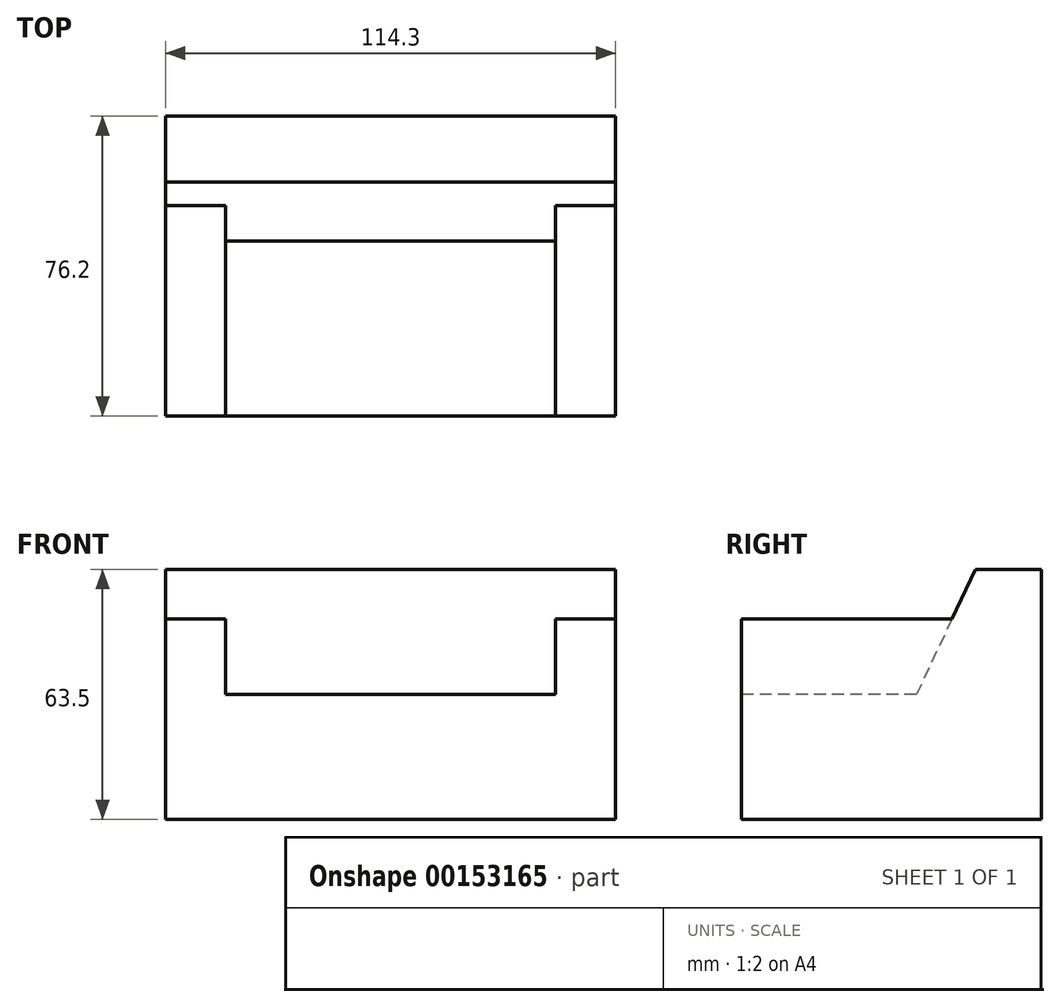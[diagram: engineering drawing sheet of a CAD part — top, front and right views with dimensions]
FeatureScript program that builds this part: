
annotation { "Feature Type Name" : "Feature", "Feature Type Description" : "" }
export const myFeature = defineFeature(function(context is Context, id is Id, definition is map)
    precondition{}
    {
        {
            var Q0;
            Q0=qCreatedBy(makeId("Right.planeOp"),FACE);
            var sketch = newSketch(context, id + "F0", { "sketchPlane" : qUnion([Q0])});
            skLineSegment(sketch, "E0", {"start": v(0, 0) * mm, "end": v(0, 63.5) * mm});
            skLineSegment(sketch, "E1", {"start": v(0, 63.5) * mm, "end": v(-16.76, 63.5) * mm});
            skLineSegment(sketch, "E2", {"start": v(-16.76, 63.5) * mm, "end": v(-31.75, 31.75) * mm});
            skLineSegment(sketch, "E3", {"start": v(-31.75, 31.75) * mm, "end": v(-76.2, 31.75) * mm});
            skLineSegment(sketch, "E4", {"start": v(-76.2, 31.75) * mm, "end": v(-76.2, 0) * mm});
            skLineSegment(sketch, "E5", {"start": v(-76.2, 0) * mm, "end": v(0, 0) * mm});
            skSolve(sketch);
        }
        {
            var Q0;
            Q0=qSketchRegion(id+"F0",true);
            extrude(context, id + "F1", {"entities" : qUnion([Q0]), "endBound" : BoundingType.SYMMETRIC, "depth" : 114.3 * mm});
        }
        {
            var Q0;
            Q0=makeQuery(id+"F1.opExtrude","CAP_FACE",FACE,{"disambiguationData":[OSD([sQuery(id+"F0.wireOp",EDGE,"E0"),sQuery(id+"F0.wireOp",EDGE,"E1"),sQuery(id+"F0.wireOp",EDGE,"E2"),sQuery(id+"F0.wireOp",EDGE,"E3"),sQuery(id+"F0.wireOp",EDGE,"E4"),sQuery(id+"F0.wireOp",EDGE,"E5")])],"isStart":false});
            var sketch = newSketch(context, id + "F2", { "sketchPlane" : qUnion([Q0])});
            skLineSegment(sketch, "E6", {"start": v(-76.2, 0) * mm, "end": v(-76.2, 50.96) * mm});
            skLineSegment(sketch, "E7", {"start": v(-76.2, 50.96) * mm, "end": v(0, 50.96) * mm});
            skLineSegment(sketch, "E8", {"start": v(0, 50.96) * mm, "end": v(0, 0) * mm});
            skLineSegment(sketch, "E9", {"start": v(0, 0) * mm, "end": v(-76.2, 0) * mm});
            skSolve(sketch);
        }
        {
            var Q0;
            Q0=qSketchRegion(id+"F2",true);
            extrude(context, id + "F3", {"entities" : qUnion([Q0]), "operationType" : NewBodyOperationType.ADD, "oppositeDirection" : true, "depth" : 15.24 * mm});
        }
        {
            var Q0;
            Q0=makeQuery(id+"F1.opExtrude","SWEPT_BODY",BODY,{"disambiguationData":[OSD([sQuery(id+"F0.wireOp",EDGE,"E0"),sQuery(id+"F0.wireOp",EDGE,"E1"),sQuery(id+"F0.wireOp",EDGE,"E2"),sQuery(id+"F0.wireOp",EDGE,"E3"),sQuery(id+"F0.wireOp",EDGE,"E4"),sQuery(id+"F0.wireOp",EDGE,"E5")])]});
            var Q1;
            Q1=qCreatedBy(makeId("Right.planeOp"),FACE);
            mirror(context, id + "F4", {"operationType" : NewBodyOperationType.ADD, "entities" : qUnion([Q0]), "mirrorPlane" : qUnion([Q1])});
        }
    });
